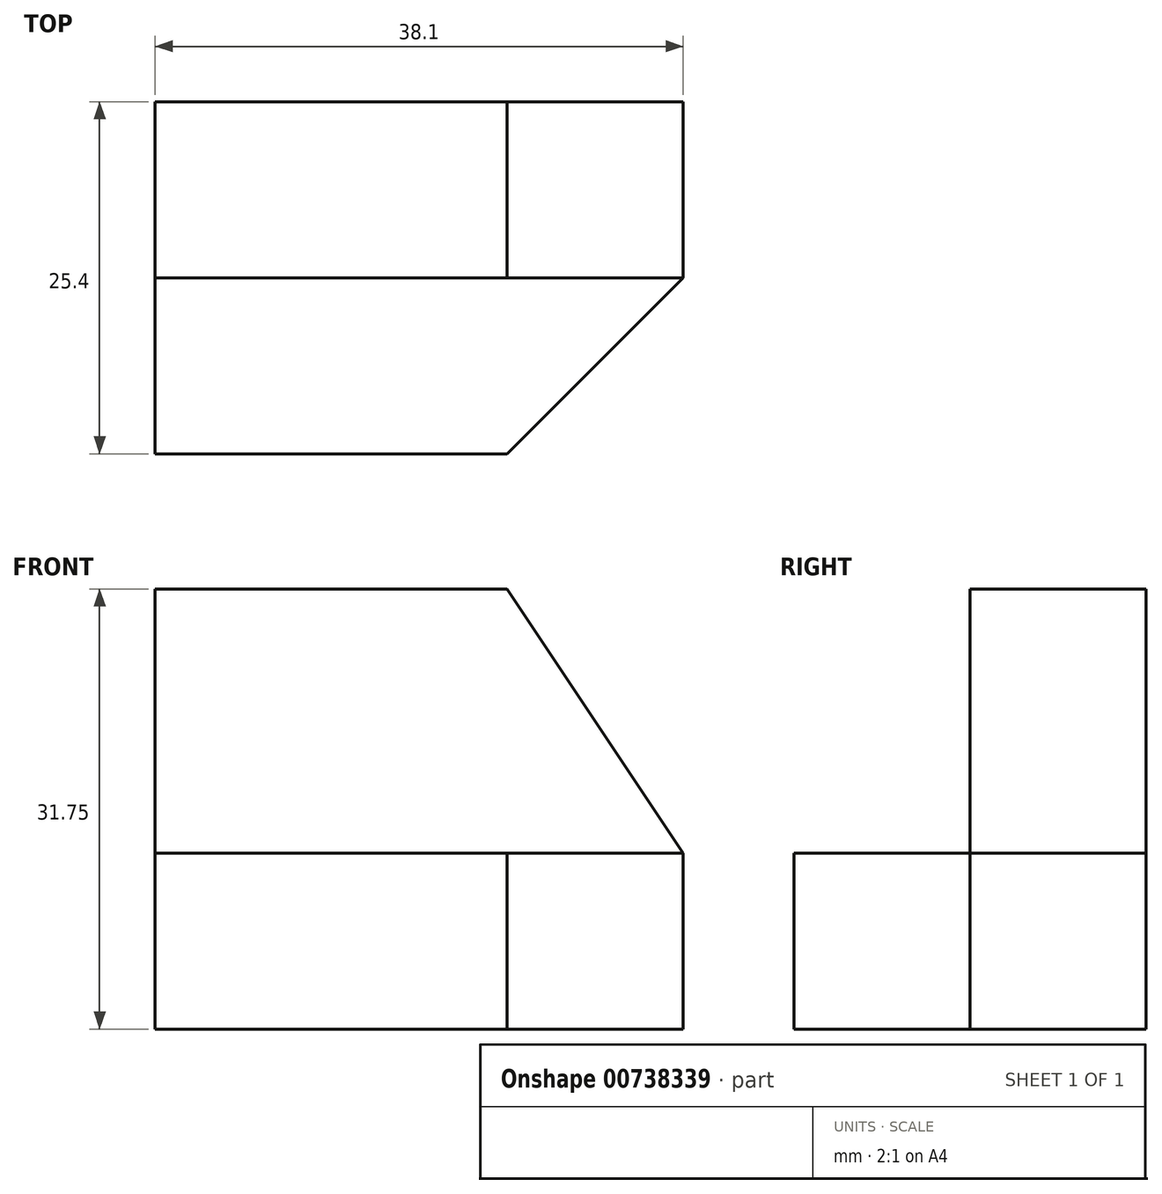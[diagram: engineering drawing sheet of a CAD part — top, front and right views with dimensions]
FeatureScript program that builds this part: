
annotation { "Feature Type Name" : "Feature", "Feature Type Description" : "" }
export const myFeature = defineFeature(function(context is Context, id is Id, definition is map)
    precondition{}
    {
        {
            var Q0;
            Q0=qCreatedBy(makeId("Right.planeOp"),FACE);
            var sketch = newSketch(context, id + "F0", { "sketchPlane" : qUnion([Q0])});
            skLineSegment(sketch, "E0", {"start": v(0, 0) * mm, "end": v(0, 31.75) * mm});
            skLineSegment(sketch, "E1", {"start": v(0, 31.75) * mm, "end": v(-12.7, 31.75) * mm});
            skLineSegment(sketch, "E2", {"start": v(-12.7, 31.75) * mm, "end": v(-12.7, 12.7) * mm});
            skLineSegment(sketch, "E3", {"start": v(-12.7, 12.7) * mm, "end": v(-25.4, 12.7) * mm});
            skLineSegment(sketch, "E4", {"start": v(-25.4, 12.7) * mm, "end": v(-25.4, 0) * mm});
            skLineSegment(sketch, "E5", {"start": v(-25.4, 0) * mm, "end": v(0, 0) * mm});
            skSolve(sketch);
        }
        {
            var Q0;
            Q0 = qSketchRegion(id + "F0", true);
            extrude(context, id + "F1", {"entities" : qUnion([Q0]), "depth" : 38.1 * mm, "offsetDistance" : 25.4 * mm});
        }
        {
            var Q0;
            Q0=makeQuery(id+"F1.opExtrude","SWEPT_FACE",FACE,{"disambiguationData":[OSD([sQuery(id+"F0.wireOp",EDGE,"E3")])]});
            var sketch = newSketch(context, id + "F2", { "sketchPlane" : qUnion([Q0])});
            skLineSegment(sketch, "E6", {"start": v(38.1, -12.7) * mm, "end": v(25.4, -25.4) * mm});
            skLineSegment(sketch, "E7", {"start": v(25.4, -25.4) * mm, "end": v(0, -25.4) * mm});
            skSolve(sketch);
        }
        {
            var Q0;
            Q0 = qSketchRegion(id + "F2", true);
            var Q1;
            {var subQ0=sQuery(id+"F2.wireOp",EDGE,"E6");Q1=makeQuery(id+"F2.imprint","IMPRINT",FACE,{"disambiguationData":[TD([[makeQuery(id+"F2.imprint","IMPRINT",EDGE,{"derivedFrom":subQ0}),1.0]])]});}
            extrude(context, id + "F3", {"entities" : qUnion([Q0, Q1]), "operationType" : NewBodyOperationType.REMOVE, "endBound" : BoundingType.THROUGH_ALL, "oppositeDirection" : true, "depth" : 25.4 * mm, "offsetDistance" : 25.4 * mm});
        }
        {
            var Q0;
            Q0=makeQuery(id+"F1.opExtrude","SWEPT_FACE",FACE,{"disambiguationData":[OSD([sQuery(id+"F0.wireOp",EDGE,"E2")])]});
            var sketch = newSketch(context, id + "F4", { "sketchPlane" : qUnion([Q0])});
            skLineSegment(sketch, "E8", {"start": v(38.1, 12.7) * mm, "end": v(25.4, 31.75) * mm});
            skLineSegment(sketch, "E9", {"start": v(25.4, 31.75) * mm, "end": v(0, 31.75) * mm});
            skSolve(sketch);
        }
        {
            var Q0;
            Q0 = qSketchRegion(id + "F4", true);
            var Q1;
            {var subQ0=sQuery(id+"F4.wireOp",EDGE,"E8");Q1=makeQuery(id+"F4.imprint","IMPRINT",FACE,{"disambiguationData":[TD([[makeQuery(id+"F4.imprint","IMPRINT",EDGE,{"derivedFrom":subQ0}),-1.0]])]});}
            extrude(context, id + "F5", {"entities" : qUnion([Q0, Q1]), "operationType" : NewBodyOperationType.REMOVE, "endBound" : BoundingType.THROUGH_ALL, "oppositeDirection" : true, "depth" : 25.4 * mm, "offsetDistance" : 25.4 * mm});
        }
    });
